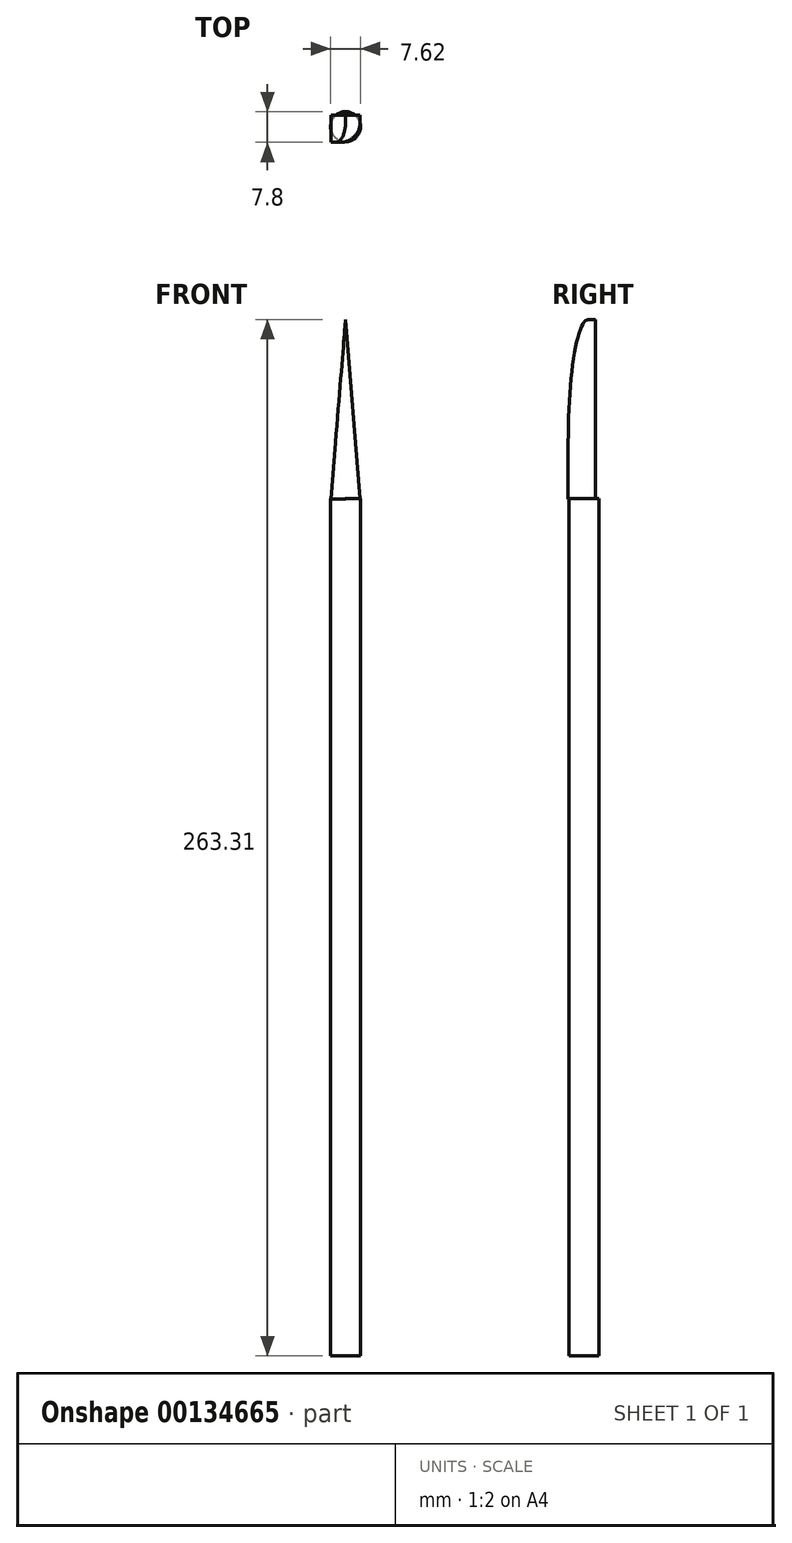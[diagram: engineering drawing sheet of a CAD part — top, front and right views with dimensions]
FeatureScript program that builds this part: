
annotation { "Feature Type Name" : "Feature", "Feature Type Description" : "" }
export const myFeature = defineFeature(function(context is Context, id is Id, definition is map)
    precondition{}
    {
        {
            var Q0;
            Q0=qCreatedBy(makeId("Top.planeOp"),FACE);
            var sketch = newSketch(context, id + "F0", { "sketchPlane" : qUnion([Q0])});
            skCircle(sketch, "E0", {"center": v(0, 0) * mm, "radius": 3.81 * mm});
            skSolve(sketch);
        }
        {
            var Q0;
            Q0 = qSketchRegion(id + "F0", true);
            extrude(context, id + "F1", {"entities" : qUnion([Q0]), "depth" : 217.85 * mm});
        }
        {
            var Q0;
            Q0=qCreatedBy(makeId("Top.planeOp"),FACE);
            var sketch = newSketch(context, id + "F2", { "sketchPlane" : qUnion([Q0])});
            skCircle(sketch, "E1", {"center": v(0, 0) * mm, "radius": 3.81 * mm});
            skSolve(sketch);
        }
        {
            var Q0;
            Q0 = qSketchRegion(id + "F2", true);
            var Q1;
            Q1=sQuery(id+"F2.wireOp",EDGE,"E1");
            extrude(context, id + "F3", {"entities" : qUnion([Q0]), "bodyType" : ToolBodyType.SURFACE, "surfaceEntities" : qUnion([Q1]), "depth" : 160.21 * mm});
        }
        {
            var Q0;
            Q0=qCreatedBy(makeId("Front.planeOp"),FACE);
            var sketch = newSketch(context, id + "F4", { "sketchPlane" : qUnion([Q0])});
            skLineSegment(sketch, "E2", {"start": v(-3.72, 217.68) * mm, "end": v(0, 263.31) * mm});
            skLineSegment(sketch, "E3", {"start": v(0, 263.31) * mm, "end": v(3.73, 217.78) * mm});
            skLineSegment(sketch, "E4", {"start": v(-3.72, 217.68) * mm, "end": v(3.73, 217.78) * mm});
            skSolve(sketch);
        }
        {
            var Q0;
            Q0 = qSketchRegion(id + "F4", true);
            extrude(context, id + "F5", {"entities" : qUnion([Q0]), "operationType" : NewBodyOperationType.ADD, "depth" : 4 * mm, "hasSecondDirection" : true, "secondDirectionOppositeDirection" : true, "secondDirectionDepth" : 2.94 * mm});
        }
        {
            var Q0;
            Q0=makeQuery(id+"F5.opExtrude","CAP_EDGE",EDGE,{"disambiguationData":[OSD([sQuery(id+"F4.wireOp",EDGE,"E3")])],"isStart":false});
            fillet(context, id + "F6", {"entities" : qUnion([Q0]), "radius" : 5.08 * mm, "tangentPropagation" : true, "allowEdgeOverflow" : false});
        }
    });
